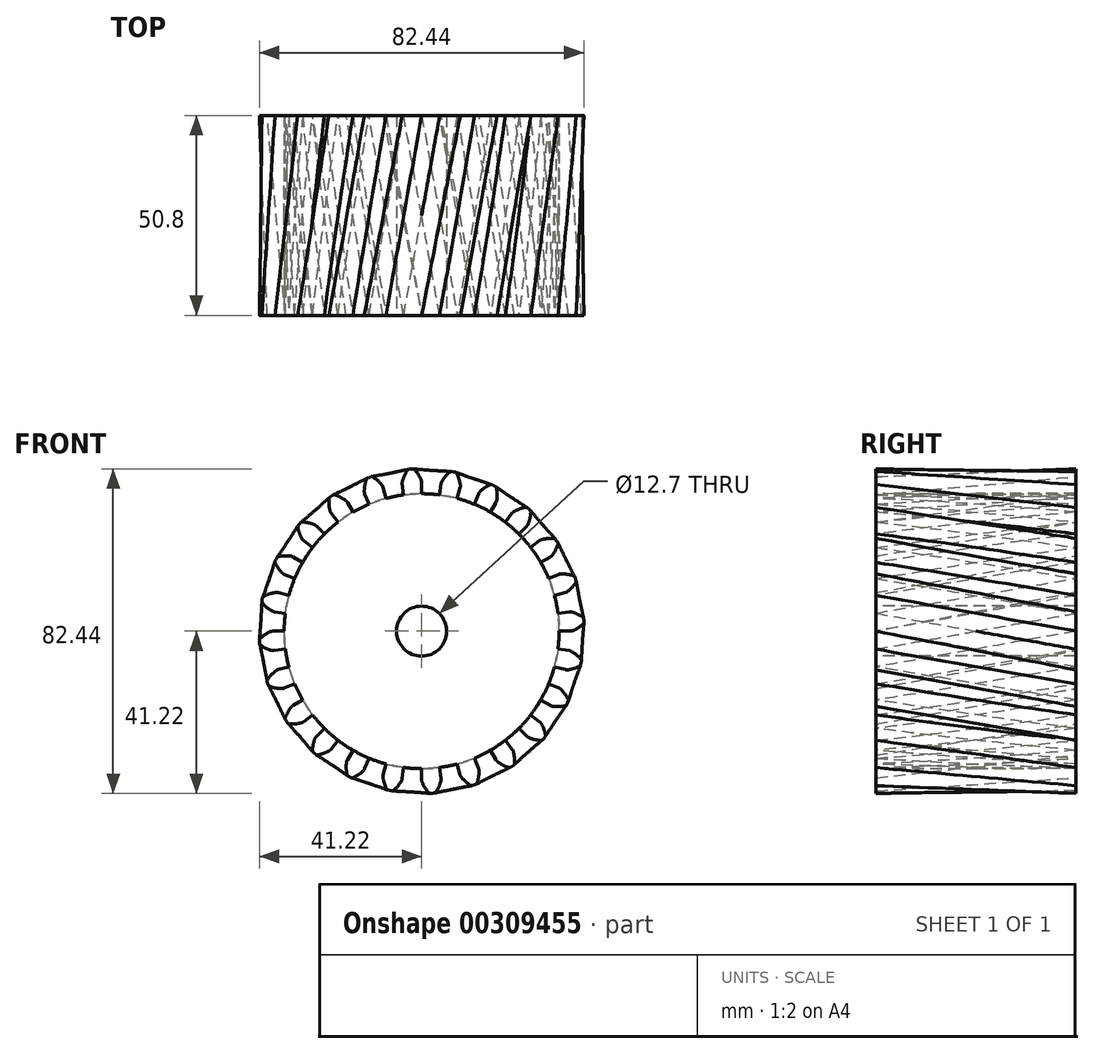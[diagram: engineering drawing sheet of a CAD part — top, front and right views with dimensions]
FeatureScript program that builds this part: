
annotation { "Feature Type Name" : "Feature", "Feature Type Description" : "" }
export const myFeature = defineFeature(function(context is Context, id is Id, definition is map)
    precondition{}
    {
        {
            var Q0;
            Q0=qCreatedBy(makeId("Front.planeOp"),FACE);
            var sketch = newSketch(context, id + "F0", { "sketchPlane" : qUnion([Q0])});
            skCircle(sketch, "E0", {"center": v(0, 0) * mm, "radius": 34.92 * mm});
            skArc(sketch, "E1", {"start": v(-0.13, 38.42) * mm, "mid": v(-0.86, 39.8) * mm, "end": v(-1.8, 41.05) * mm});
            skLineSegment(sketch, "E2", {"start": v(-2.2, 41.22) * mm, "end": v(-2.7, 41.2) * mm});
            skLineSegment(sketch, "E3", {"start": v(0, 37.79) * mm, "end": v(0, 34.92) * mm});
            skLineSegment(sketch, "E4.MirrorCS", {"start": v(-3.2, 41.15) * mm, "end": v(-2.7, 41.2) * mm});
            skArc(sketch, "E5.MirrorCS", {"start": v(-4.89, 38.1) * mm, "mid": v(-4.34, 39.57) * mm, "end": v(-3.57, 40.93) * mm});
            skLineSegment(sketch, "E6.MirrorCS", {"start": v(-4.93, 37.47) * mm, "end": v(-4.56, 34.63) * mm});
            skPoint(sketch, "E7.visualSharp", {"position": v(-4.97, 37.77) * mm});
            skArc(sketch, "E7.filletArc", {"start": v(-4.89, 38.1) * mm, "mid": v(-4.94, 37.79) * mm, "end": v(-4.93, 37.47) * mm});
            skPoint(sketch, "E8.visualSharp", {"position": v(0, 38.1) * mm});
            skArc(sketch, "E8.filletArc", {"start": v(0, 37.79) * mm, "mid": v(-0.03, 38.1) * mm, "end": v(-0.13, 38.42) * mm});
            skPoint(sketch, "E9.visualSharp", {"position": v(-3.43, 41.13) * mm});
            skArc(sketch, "E9.filletArc", {"start": v(-3.2, 41.15) * mm, "mid": v(-3.4, 41.09) * mm, "end": v(-3.57, 40.93) * mm});
            skPoint(sketch, "E10.visualSharp", {"position": v(-1.97, 41.23) * mm});
            skArc(sketch, "E10.filletArc", {"start": v(-1.8, 41.05) * mm, "mid": v(-1.99, 41.18) * mm, "end": v(-2.2, 41.22) * mm});
            skSolve(sketch);
        }
        {
            var Q0;
            Q0=qCreatedBy(makeId("Front.planeOp"),FACE);
            cPlane(context, id + "F1", {"entities" : qUnion([Q0]), "cplaneType" : CPlaneType.OFFSET, "offset" : 50.8 * mm, "width" : 152.4 * mm, "height" : 152.4 * mm});
        }
        {
            var Q0;
            Q0=qCreatedBy(id+"F1.planeOp",FACE);
            var sketch = newSketch(context, id + "F2", { "sketchPlane" : qUnion([Q0])});
            skCircle(sketch, "E11", {"center": v(0, 0) * mm, "radius": 34.92 * mm});
            skArc(sketch, "E12", {"start": v(-0.13, 38.42) * mm, "mid": v(-0.86, 39.8) * mm, "end": v(-1.8, 41.05) * mm});
            skLineSegment(sketch, "E13", {"start": v(-2.2, 41.22) * mm, "end": v(-2.7, 41.2) * mm});
            skLineSegment(sketch, "E14", {"start": v(0, 37.79) * mm, "end": v(0, 34.92) * mm});
            skLineSegment(sketch, "E15.MirrorCS", {"start": v(-3.2, 41.15) * mm, "end": v(-2.7, 41.2) * mm});
            skArc(sketch, "E16.MirrorCS", {"start": v(-4.89, 38.1) * mm, "mid": v(-4.34, 39.57) * mm, "end": v(-3.57, 40.93) * mm});
            skLineSegment(sketch, "E17.MirrorCS", {"start": v(-4.93, 37.47) * mm, "end": v(-4.56, 34.63) * mm});
            skPoint(sketch, "E18.visualSharp", {"position": v(-4.97, 37.77) * mm});
            skArc(sketch, "E18.filletArc", {"start": v(-4.89, 38.1) * mm, "mid": v(-4.94, 37.79) * mm, "end": v(-4.93, 37.47) * mm});
            skPoint(sketch, "E19.visualSharp", {"position": v(0, 38.1) * mm});
            skArc(sketch, "E19.filletArc", {"start": v(0, 37.79) * mm, "mid": v(-0.03, 38.1) * mm, "end": v(-0.13, 38.42) * mm});
            skPoint(sketch, "E20.visualSharp", {"position": v(-3.43, 41.13) * mm});
            skArc(sketch, "E20.filletArc", {"start": v(-3.2, 41.15) * mm, "mid": v(-3.4, 41.09) * mm, "end": v(-3.57, 40.93) * mm});
            skPoint(sketch, "E21.visualSharp", {"position": v(-1.97, 41.23) * mm});
            skArc(sketch, "E21.filletArc", {"start": v(-1.8, 41.05) * mm, "mid": v(-1.99, 41.18) * mm, "end": v(-2.2, 41.22) * mm});
            skLineSegment(sketch, "E22.1.0", {"start": v(-13.73, 38.92) * mm, "end": v(-13.27, 39.1) * mm});
            skLineSegment(sketch, "E22.1.1", {"start": v(-12.8, 39.24) * mm, "end": v(-13.27, 39.1) * mm});
            skArc(sketch, "E22.1.2", {"start": v(-13.73, 38.92) * mm, "mid": v(-13.92, 38.8) * mm, "end": v(-14.04, 38.62) * mm});
            skArc(sketch, "E22.1.3", {"start": v(-12.37, 39.18) * mm, "mid": v(-12.58, 39.26) * mm, "end": v(-12.8, 39.24) * mm});
            skArc(sketch, "E22.1.4", {"start": v(-14.58, 35.54) * mm, "mid": v(-14.44, 37.1) * mm, "end": v(-14.04, 38.62) * mm});
            skArc(sketch, "E22.1.5", {"start": v(-10.07, 37.07) * mm, "mid": v(-11.13, 38.22) * mm, "end": v(-12.37, 39.18) * mm});
            skArc(sketch, "E22.1.6", {"start": v(-14.58, 35.54) * mm, "mid": v(-14.55, 35.22) * mm, "end": v(-14.46, 34.91) * mm});
            skArc(sketch, "E22.1.7", {"start": v(-9.78, 36.5) * mm, "mid": v(-9.9, 36.8) * mm, "end": v(-10.07, 37.07) * mm});
            skLineSegment(sketch, "E22.1.8", {"start": v(-9.78, 36.5) * mm, "end": v(-9.04, 33.73) * mm});
            skLineSegment(sketch, "E22.1.9", {"start": v(-14.46, 34.91) * mm, "end": v(-13.37, 32.27) * mm});
            skLineSegment(sketch, "E22.2.0", {"start": v(-23.34, 34.04) * mm, "end": v(-22.93, 34.32) * mm});
            skLineSegment(sketch, "E22.2.1", {"start": v(-22.52, 34.6) * mm, "end": v(-22.93, 34.32) * mm});
            skArc(sketch, "E22.2.2", {"start": v(-23.34, 34.04) * mm, "mid": v(-23.49, 33.88) * mm, "end": v(-23.56, 33.67) * mm});
            skArc(sketch, "E22.2.3", {"start": v(-22.09, 34.65) * mm, "mid": v(-22.31, 34.67) * mm, "end": v(-22.52, 34.6) * mm});
            skArc(sketch, "E22.2.4", {"start": v(-23.28, 30.56) * mm, "mid": v(-23.55, 32.1) * mm, "end": v(-23.56, 33.67) * mm});
            skArc(sketch, "E22.2.5", {"start": v(-19.32, 33.2) * mm, "mid": v(-20.64, 34.04) * mm, "end": v(-22.09, 34.65) * mm});
            skArc(sketch, "E22.2.6", {"start": v(-23.28, 30.56) * mm, "mid": v(-23.17, 30.25) * mm, "end": v(-23, 29.98) * mm});
            skArc(sketch, "E22.2.7", {"start": v(-18.9, 32.73) * mm, "mid": v(-19.08, 32.99) * mm, "end": v(-19.32, 33.2) * mm});
            skLineSegment(sketch, "E22.2.8", {"start": v(-18.9, 32.73) * mm, "end": v(-17.46, 30.25) * mm});
            skLineSegment(sketch, "E22.2.9", {"start": v(-23, 29.98) * mm, "end": v(-21.26, 27.7) * mm});
            skLineSegment(sketch, "E22.3.0", {"start": v(-31.35, 26.84) * mm, "end": v(-31.04, 27.22) * mm});
            skLineSegment(sketch, "E22.3.1", {"start": v(-30.7, 27.58) * mm, "end": v(-31.04, 27.22) * mm});
            skArc(sketch, "E22.3.2", {"start": v(-31.35, 26.84) * mm, "mid": v(-31.46, 26.65) * mm, "end": v(-31.47, 26.42) * mm});
            skArc(sketch, "E22.3.3", {"start": v(-30.3, 27.75) * mm, "mid": v(-30.52, 27.71) * mm, "end": v(-30.7, 27.58) * mm});
            skArc(sketch, "E22.3.4", {"start": v(-30.4, 23.49) * mm, "mid": v(-31.05, 24.91) * mm, "end": v(-31.47, 26.42) * mm});
            skArc(sketch, "E22.3.5", {"start": v(-27.26, 27.07) * mm, "mid": v(-28.75, 27.54) * mm, "end": v(-30.3, 27.75) * mm});
            skArc(sketch, "E22.3.6", {"start": v(-30.4, 23.49) * mm, "mid": v(-30.21, 23.22) * mm, "end": v(-29.98, 23) * mm});
            skArc(sketch, "E22.3.7", {"start": v(-26.72, 26.72) * mm, "mid": v(-26.97, 26.92) * mm, "end": v(-27.26, 27.07) * mm});
            skLineSegment(sketch, "E22.3.8", {"start": v(-26.72, 26.72) * mm, "end": v(-24.7, 24.7) * mm});
            skLineSegment(sketch, "E22.3.9", {"start": v(-29.98, 23) * mm, "end": v(-27.7, 21.26) * mm});
            skLineSegment(sketch, "E22.4.0", {"start": v(-37.23, 17.81) * mm, "end": v(-37.02, 18.26) * mm});
            skLineSegment(sketch, "E22.4.1", {"start": v(-36.8, 18.7) * mm, "end": v(-37.02, 18.26) * mm});
            skArc(sketch, "E22.4.2", {"start": v(-37.23, 17.81) * mm, "mid": v(-37.28, 17.6) * mm, "end": v(-37.23, 17.38) * mm});
            skArc(sketch, "E22.4.3", {"start": v(-36.45, 18.96) * mm, "mid": v(-36.66, 18.87) * mm, "end": v(-36.8, 18.7) * mm});
            skArc(sketch, "E22.4.4", {"start": v(-35.44, 14.82) * mm, "mid": v(-36.44, 16.02) * mm, "end": v(-37.23, 17.38) * mm});
            skArc(sketch, "E22.4.5", {"start": v(-33.33, 19.1) * mm, "mid": v(-34.9, 19.16) * mm, "end": v(-36.45, 18.96) * mm});
            skArc(sketch, "E22.4.6", {"start": v(-35.44, 14.82) * mm, "mid": v(-35.2, 14.61) * mm, "end": v(-34.91, 14.46) * mm});
            skArc(sketch, "E22.4.7", {"start": v(-32.73, 18.9) * mm, "mid": v(-33.02, 19.03) * mm, "end": v(-33.33, 19.1) * mm});
            skLineSegment(sketch, "E22.4.8", {"start": v(-32.73, 18.9) * mm, "end": v(-30.25, 17.46) * mm});
            skLineSegment(sketch, "E22.4.9", {"start": v(-34.91, 14.46) * mm, "end": v(-32.27, 13.37) * mm});
            skLineSegment(sketch, "E22.5.0", {"start": v(-40.58, 7.57) * mm, "end": v(-40.49, 8.05) * mm});
            skLineSegment(sketch, "E22.5.1", {"start": v(-40.38, 8.53) * mm, "end": v(-40.49, 8.05) * mm});
            skArc(sketch, "E22.5.2", {"start": v(-40.58, 7.57) * mm, "mid": v(-40.57, 7.35) * mm, "end": v(-40.46, 7.15) * mm});
            skArc(sketch, "E22.5.3", {"start": v(-40.12, 8.88) * mm, "mid": v(-40.29, 8.74) * mm, "end": v(-40.38, 8.53) * mm});
            skArc(sketch, "E22.5.4", {"start": v(-38.07, 5.14) * mm, "mid": v(-39.35, 6.05) * mm, "end": v(-40.46, 7.15) * mm});
            skArc(sketch, "E22.5.5", {"start": v(-37.14, 9.82) * mm, "mid": v(-38.67, 9.47) * mm, "end": v(-40.12, 8.88) * mm});
            skArc(sketch, "E22.5.6", {"start": v(-38.07, 5.14) * mm, "mid": v(-37.78, 5) * mm, "end": v(-37.47, 4.93) * mm});
            skArc(sketch, "E22.5.7", {"start": v(-36.5, 9.78) * mm, "mid": v(-36.82, 9.83) * mm, "end": v(-37.14, 9.82) * mm});
            skLineSegment(sketch, "E22.5.8", {"start": v(-36.5, 9.78) * mm, "end": v(-33.73, 9.04) * mm});
            skLineSegment(sketch, "E22.5.9", {"start": v(-37.47, 4.93) * mm, "end": v(-34.63, 4.56) * mm});
            skLineSegment(sketch, "E22.6.0", {"start": v(-41.15, -3.2) * mm, "end": v(-41.2, -2.7) * mm});
            skLineSegment(sketch, "E22.6.1", {"start": v(-41.22, -2.2) * mm, "end": v(-41.2, -2.7) * mm});
            skArc(sketch, "E22.6.2", {"start": v(-41.15, -3.2) * mm, "mid": v(-41.09, -3.4) * mm, "end": v(-40.93, -3.57) * mm});
            skArc(sketch, "E22.6.3", {"start": v(-41.05, -1.8) * mm, "mid": v(-41.18, -1.99) * mm, "end": v(-41.22, -2.2) * mm});
            skArc(sketch, "E22.6.4", {"start": v(-38.1, -4.89) * mm, "mid": v(-39.57, -4.34) * mm, "end": v(-40.93, -3.57) * mm});
            skArc(sketch, "E22.6.5", {"start": v(-38.42, -0.13) * mm, "mid": v(-39.8, -0.86) * mm, "end": v(-41.05, -1.8) * mm});
            skArc(sketch, "E22.6.6", {"start": v(-38.1, -4.89) * mm, "mid": v(-37.79, -4.94) * mm, "end": v(-37.47, -4.93) * mm});
            skArc(sketch, "E22.6.7", {"start": v(-37.79, 0) * mm, "mid": v(-38.1, -0.03) * mm, "end": v(-38.42, -0.13) * mm});
            skLineSegment(sketch, "E22.6.8", {"start": v(-37.79, 0) * mm, "end": v(-34.92, 0) * mm});
            skLineSegment(sketch, "E22.6.9", {"start": v(-37.47, -4.93) * mm, "end": v(-34.63, -4.56) * mm});
            skLineSegment(sketch, "E22.7.0", {"start": v(-38.92, -13.73) * mm, "end": v(-39.1, -13.27) * mm});
            skLineSegment(sketch, "E22.7.1", {"start": v(-39.24, -12.8) * mm, "end": v(-39.1, -13.27) * mm});
            skArc(sketch, "E22.7.2", {"start": v(-38.92, -13.73) * mm, "mid": v(-38.8, -13.92) * mm, "end": v(-38.62, -14.04) * mm});
            skArc(sketch, "E22.7.3", {"start": v(-39.18, -12.37) * mm, "mid": v(-39.26, -12.58) * mm, "end": v(-39.24, -12.8) * mm});
            skArc(sketch, "E22.7.4", {"start": v(-35.54, -14.58) * mm, "mid": v(-37.1, -14.44) * mm, "end": v(-38.62, -14.04) * mm});
            skArc(sketch, "E22.7.5", {"start": v(-37.07, -10.07) * mm, "mid": v(-38.22, -11.13) * mm, "end": v(-39.18, -12.37) * mm});
            skArc(sketch, "E22.7.6", {"start": v(-35.54, -14.58) * mm, "mid": v(-35.22, -14.55) * mm, "end": v(-34.91, -14.46) * mm});
            skArc(sketch, "E22.7.7", {"start": v(-36.5, -9.78) * mm, "mid": v(-36.8, -9.9) * mm, "end": v(-37.07, -10.07) * mm});
            skLineSegment(sketch, "E22.7.8", {"start": v(-36.5, -9.78) * mm, "end": v(-33.73, -9.04) * mm});
            skLineSegment(sketch, "E22.7.9", {"start": v(-34.91, -14.46) * mm, "end": v(-32.27, -13.37) * mm});
            skLineSegment(sketch, "E22.8.0", {"start": v(-34.04, -23.34) * mm, "end": v(-34.32, -22.93) * mm});
            skLineSegment(sketch, "E22.8.1", {"start": v(-34.6, -22.52) * mm, "end": v(-34.32, -22.93) * mm});
            skArc(sketch, "E22.8.2", {"start": v(-34.04, -23.34) * mm, "mid": v(-33.88, -23.49) * mm, "end": v(-33.67, -23.56) * mm});
            skArc(sketch, "E22.8.3", {"start": v(-34.65, -22.09) * mm, "mid": v(-34.67, -22.31) * mm, "end": v(-34.6, -22.52) * mm});
            skArc(sketch, "E22.8.4", {"start": v(-30.56, -23.28) * mm, "mid": v(-32.1, -23.55) * mm, "end": v(-33.67, -23.56) * mm});
            skArc(sketch, "E22.8.5", {"start": v(-33.2, -19.32) * mm, "mid": v(-34.04, -20.64) * mm, "end": v(-34.65, -22.09) * mm});
            skArc(sketch, "E22.8.6", {"start": v(-30.56, -23.28) * mm, "mid": v(-30.25, -23.17) * mm, "end": v(-29.98, -23) * mm});
            skArc(sketch, "E22.8.7", {"start": v(-32.73, -18.9) * mm, "mid": v(-32.99, -19.08) * mm, "end": v(-33.2, -19.32) * mm});
            skLineSegment(sketch, "E22.8.8", {"start": v(-32.73, -18.9) * mm, "end": v(-30.25, -17.46) * mm});
            skLineSegment(sketch, "E22.8.9", {"start": v(-29.98, -23) * mm, "end": v(-27.7, -21.26) * mm});
            skLineSegment(sketch, "E22.9.0", {"start": v(-26.84, -31.35) * mm, "end": v(-27.22, -31.04) * mm});
            skLineSegment(sketch, "E22.9.1", {"start": v(-27.58, -30.7) * mm, "end": v(-27.22, -31.04) * mm});
            skArc(sketch, "E22.9.2", {"start": v(-26.84, -31.35) * mm, "mid": v(-26.65, -31.46) * mm, "end": v(-26.42, -31.47) * mm});
            skArc(sketch, "E22.9.3", {"start": v(-27.75, -30.3) * mm, "mid": v(-27.71, -30.52) * mm, "end": v(-27.58, -30.7) * mm});
            skArc(sketch, "E22.9.4", {"start": v(-23.49, -30.4) * mm, "mid": v(-24.91, -31.05) * mm, "end": v(-26.42, -31.47) * mm});
            skArc(sketch, "E22.9.5", {"start": v(-27.07, -27.26) * mm, "mid": v(-27.54, -28.75) * mm, "end": v(-27.75, -30.3) * mm});
            skArc(sketch, "E22.9.6", {"start": v(-23.49, -30.4) * mm, "mid": v(-23.22, -30.21) * mm, "end": v(-23, -29.98) * mm});
            skArc(sketch, "E22.9.7", {"start": v(-26.72, -26.72) * mm, "mid": v(-26.92, -26.97) * mm, "end": v(-27.07, -27.26) * mm});
            skLineSegment(sketch, "E22.9.8", {"start": v(-26.72, -26.72) * mm, "end": v(-24.7, -24.7) * mm});
            skLineSegment(sketch, "E22.9.9", {"start": v(-23, -29.98) * mm, "end": v(-21.26, -27.7) * mm});
            skLineSegment(sketch, "E22.10.0", {"start": v(-17.81, -37.23) * mm, "end": v(-18.26, -37.02) * mm});
            skLineSegment(sketch, "E22.10.1", {"start": v(-18.7, -36.8) * mm, "end": v(-18.26, -37.02) * mm});
            skArc(sketch, "E22.10.2", {"start": v(-17.81, -37.23) * mm, "mid": v(-17.6, -37.28) * mm, "end": v(-17.38, -37.23) * mm});
            skArc(sketch, "E22.10.3", {"start": v(-18.96, -36.45) * mm, "mid": v(-18.87, -36.66) * mm, "end": v(-18.7, -36.8) * mm});
            skArc(sketch, "E22.10.4", {"start": v(-14.82, -35.44) * mm, "mid": v(-16.02, -36.44) * mm, "end": v(-17.38, -37.23) * mm});
            skArc(sketch, "E22.10.5", {"start": v(-19.1, -33.33) * mm, "mid": v(-19.16, -34.9) * mm, "end": v(-18.96, -36.45) * mm});
            skArc(sketch, "E22.10.6", {"start": v(-14.82, -35.44) * mm, "mid": v(-14.61, -35.2) * mm, "end": v(-14.46, -34.91) * mm});
            skArc(sketch, "E22.10.7", {"start": v(-18.9, -32.73) * mm, "mid": v(-19.03, -33.02) * mm, "end": v(-19.1, -33.33) * mm});
            skLineSegment(sketch, "E22.10.8", {"start": v(-18.9, -32.73) * mm, "end": v(-17.46, -30.25) * mm});
            skLineSegment(sketch, "E22.10.9", {"start": v(-14.46, -34.91) * mm, "end": v(-13.37, -32.27) * mm});
            skLineSegment(sketch, "E22.11.0", {"start": v(-7.57, -40.58) * mm, "end": v(-8.05, -40.49) * mm});
            skLineSegment(sketch, "E22.11.1", {"start": v(-8.53, -40.38) * mm, "end": v(-8.05, -40.49) * mm});
            skArc(sketch, "E22.11.2", {"start": v(-7.57, -40.58) * mm, "mid": v(-7.35, -40.57) * mm, "end": v(-7.15, -40.46) * mm});
            skArc(sketch, "E22.11.3", {"start": v(-8.88, -40.12) * mm, "mid": v(-8.74, -40.29) * mm, "end": v(-8.53, -40.38) * mm});
            skArc(sketch, "E22.11.4", {"start": v(-5.14, -38.07) * mm, "mid": v(-6.05, -39.35) * mm, "end": v(-7.15, -40.46) * mm});
            skArc(sketch, "E22.11.5", {"start": v(-9.82, -37.14) * mm, "mid": v(-9.47, -38.67) * mm, "end": v(-8.88, -40.12) * mm});
            skArc(sketch, "E22.11.6", {"start": v(-5.14, -38.07) * mm, "mid": v(-5, -37.78) * mm, "end": v(-4.93, -37.47) * mm});
            skArc(sketch, "E22.11.7", {"start": v(-9.78, -36.5) * mm, "mid": v(-9.83, -36.82) * mm, "end": v(-9.82, -37.14) * mm});
            skLineSegment(sketch, "E22.11.8", {"start": v(-9.78, -36.5) * mm, "end": v(-9.04, -33.73) * mm});
            skLineSegment(sketch, "E22.11.9", {"start": v(-4.93, -37.47) * mm, "end": v(-4.56, -34.63) * mm});
            skLineSegment(sketch, "E22.12.0", {"start": v(3.2, -41.15) * mm, "end": v(2.7, -41.2) * mm});
            skLineSegment(sketch, "E22.12.1", {"start": v(2.2, -41.22) * mm, "end": v(2.7, -41.2) * mm});
            skArc(sketch, "E22.12.2", {"start": v(3.2, -41.15) * mm, "mid": v(3.4, -41.09) * mm, "end": v(3.57, -40.93) * mm});
            skArc(sketch, "E22.12.3", {"start": v(1.8, -41.05) * mm, "mid": v(1.99, -41.18) * mm, "end": v(2.2, -41.22) * mm});
            skArc(sketch, "E22.12.4", {"start": v(4.89, -38.1) * mm, "mid": v(4.34, -39.57) * mm, "end": v(3.57, -40.93) * mm});
            skArc(sketch, "E22.12.5", {"start": v(0.13, -38.42) * mm, "mid": v(0.86, -39.8) * mm, "end": v(1.8, -41.05) * mm});
            skArc(sketch, "E22.12.6", {"start": v(4.89, -38.1) * mm, "mid": v(4.94, -37.79) * mm, "end": v(4.93, -37.47) * mm});
            skArc(sketch, "E22.12.7", {"start": v(0, -37.79) * mm, "mid": v(0.03, -38.1) * mm, "end": v(0.13, -38.42) * mm});
            skLineSegment(sketch, "E22.12.8", {"start": v(0, -37.79) * mm, "end": v(0, -34.92) * mm});
            skLineSegment(sketch, "E22.12.9", {"start": v(4.93, -37.47) * mm, "end": v(4.56, -34.63) * mm});
            skLineSegment(sketch, "E22.13.0", {"start": v(13.73, -38.92) * mm, "end": v(13.27, -39.1) * mm});
            skLineSegment(sketch, "E22.13.1", {"start": v(12.8, -39.24) * mm, "end": v(13.27, -39.1) * mm});
            skArc(sketch, "E22.13.2", {"start": v(13.73, -38.92) * mm, "mid": v(13.92, -38.8) * mm, "end": v(14.04, -38.62) * mm});
            skArc(sketch, "E22.13.3", {"start": v(12.37, -39.18) * mm, "mid": v(12.58, -39.26) * mm, "end": v(12.8, -39.24) * mm});
            skArc(sketch, "E22.13.4", {"start": v(14.58, -35.54) * mm, "mid": v(14.44, -37.1) * mm, "end": v(14.04, -38.62) * mm});
            skArc(sketch, "E22.13.5", {"start": v(10.07, -37.07) * mm, "mid": v(11.13, -38.22) * mm, "end": v(12.37, -39.18) * mm});
            skArc(sketch, "E22.13.6", {"start": v(14.58, -35.54) * mm, "mid": v(14.55, -35.22) * mm, "end": v(14.46, -34.91) * mm});
            skArc(sketch, "E22.13.7", {"start": v(9.78, -36.5) * mm, "mid": v(9.9, -36.8) * mm, "end": v(10.07, -37.07) * mm});
            skLineSegment(sketch, "E22.13.8", {"start": v(9.78, -36.5) * mm, "end": v(9.04, -33.73) * mm});
            skLineSegment(sketch, "E22.13.9", {"start": v(14.46, -34.91) * mm, "end": v(13.37, -32.27) * mm});
            skLineSegment(sketch, "E22.14.0", {"start": v(23.34, -34.04) * mm, "end": v(22.93, -34.32) * mm});
            skLineSegment(sketch, "E22.14.1", {"start": v(22.52, -34.6) * mm, "end": v(22.93, -34.32) * mm});
            skArc(sketch, "E22.14.2", {"start": v(23.34, -34.04) * mm, "mid": v(23.49, -33.88) * mm, "end": v(23.56, -33.67) * mm});
            skArc(sketch, "E22.14.3", {"start": v(22.09, -34.65) * mm, "mid": v(22.31, -34.67) * mm, "end": v(22.52, -34.6) * mm});
            skArc(sketch, "E22.14.4", {"start": v(23.28, -30.56) * mm, "mid": v(23.55, -32.1) * mm, "end": v(23.56, -33.67) * mm});
            skArc(sketch, "E22.14.5", {"start": v(19.32, -33.2) * mm, "mid": v(20.64, -34.04) * mm, "end": v(22.09, -34.65) * mm});
            skArc(sketch, "E22.14.6", {"start": v(23.28, -30.56) * mm, "mid": v(23.17, -30.25) * mm, "end": v(23, -29.98) * mm});
            skArc(sketch, "E22.14.7", {"start": v(18.9, -32.73) * mm, "mid": v(19.08, -32.99) * mm, "end": v(19.32, -33.2) * mm});
            skLineSegment(sketch, "E22.14.8", {"start": v(18.9, -32.73) * mm, "end": v(17.46, -30.25) * mm});
            skLineSegment(sketch, "E22.14.9", {"start": v(23, -29.98) * mm, "end": v(21.26, -27.7) * mm});
            skLineSegment(sketch, "E22.15.0", {"start": v(31.35, -26.84) * mm, "end": v(31.04, -27.22) * mm});
            skLineSegment(sketch, "E22.15.1", {"start": v(30.7, -27.58) * mm, "end": v(31.04, -27.22) * mm});
            skArc(sketch, "E22.15.2", {"start": v(31.35, -26.84) * mm, "mid": v(31.46, -26.65) * mm, "end": v(31.47, -26.42) * mm});
            skArc(sketch, "E22.15.3", {"start": v(30.3, -27.75) * mm, "mid": v(30.52, -27.71) * mm, "end": v(30.7, -27.58) * mm});
            skArc(sketch, "E22.15.4", {"start": v(30.4, -23.49) * mm, "mid": v(31.05, -24.91) * mm, "end": v(31.47, -26.42) * mm});
            skArc(sketch, "E22.15.5", {"start": v(27.26, -27.07) * mm, "mid": v(28.75, -27.54) * mm, "end": v(30.3, -27.75) * mm});
            skArc(sketch, "E22.15.6", {"start": v(30.4, -23.49) * mm, "mid": v(30.21, -23.22) * mm, "end": v(29.98, -23) * mm});
            skArc(sketch, "E22.15.7", {"start": v(26.72, -26.72) * mm, "mid": v(26.97, -26.92) * mm, "end": v(27.26, -27.07) * mm});
            skLineSegment(sketch, "E22.15.8", {"start": v(26.72, -26.72) * mm, "end": v(24.7, -24.7) * mm});
            skLineSegment(sketch, "E22.15.9", {"start": v(29.98, -23) * mm, "end": v(27.7, -21.26) * mm});
            skLineSegment(sketch, "E22.16.0", {"start": v(37.23, -17.81) * mm, "end": v(37.02, -18.26) * mm});
            skLineSegment(sketch, "E22.16.1", {"start": v(36.8, -18.7) * mm, "end": v(37.02, -18.26) * mm});
            skArc(sketch, "E22.16.2", {"start": v(37.23, -17.81) * mm, "mid": v(37.28, -17.6) * mm, "end": v(37.23, -17.38) * mm});
            skArc(sketch, "E22.16.3", {"start": v(36.45, -18.96) * mm, "mid": v(36.66, -18.87) * mm, "end": v(36.8, -18.7) * mm});
            skArc(sketch, "E22.16.4", {"start": v(35.44, -14.82) * mm, "mid": v(36.44, -16.02) * mm, "end": v(37.23, -17.38) * mm});
            skArc(sketch, "E22.16.5", {"start": v(33.33, -19.1) * mm, "mid": v(34.9, -19.16) * mm, "end": v(36.45, -18.96) * mm});
            skArc(sketch, "E22.16.6", {"start": v(35.44, -14.82) * mm, "mid": v(35.2, -14.61) * mm, "end": v(34.91, -14.46) * mm});
            skArc(sketch, "E22.16.7", {"start": v(32.73, -18.9) * mm, "mid": v(33.02, -19.03) * mm, "end": v(33.33, -19.1) * mm});
            skLineSegment(sketch, "E22.16.8", {"start": v(32.73, -18.9) * mm, "end": v(30.25, -17.46) * mm});
            skLineSegment(sketch, "E22.16.9", {"start": v(34.91, -14.46) * mm, "end": v(32.27, -13.37) * mm});
            skLineSegment(sketch, "E22.17.0", {"start": v(40.58, -7.57) * mm, "end": v(40.49, -8.05) * mm});
            skLineSegment(sketch, "E22.17.1", {"start": v(40.38, -8.53) * mm, "end": v(40.49, -8.05) * mm});
            skArc(sketch, "E22.17.2", {"start": v(40.58, -7.57) * mm, "mid": v(40.57, -7.35) * mm, "end": v(40.46, -7.15) * mm});
            skArc(sketch, "E22.17.3", {"start": v(40.12, -8.88) * mm, "mid": v(40.29, -8.74) * mm, "end": v(40.38, -8.53) * mm});
            skArc(sketch, "E22.17.4", {"start": v(38.07, -5.14) * mm, "mid": v(39.35, -6.05) * mm, "end": v(40.46, -7.15) * mm});
            skArc(sketch, "E22.17.5", {"start": v(37.14, -9.82) * mm, "mid": v(38.67, -9.47) * mm, "end": v(40.12, -8.88) * mm});
            skArc(sketch, "E22.17.6", {"start": v(38.07, -5.14) * mm, "mid": v(37.78, -5) * mm, "end": v(37.47, -4.93) * mm});
            skArc(sketch, "E22.17.7", {"start": v(36.5, -9.78) * mm, "mid": v(36.82, -9.83) * mm, "end": v(37.14, -9.82) * mm});
            skLineSegment(sketch, "E22.17.8", {"start": v(36.5, -9.78) * mm, "end": v(33.73, -9.04) * mm});
            skLineSegment(sketch, "E22.17.9", {"start": v(37.47, -4.93) * mm, "end": v(34.63, -4.56) * mm});
            skLineSegment(sketch, "E22.18.0", {"start": v(41.15, 3.2) * mm, "end": v(41.2, 2.7) * mm});
            skLineSegment(sketch, "E22.18.1", {"start": v(41.22, 2.2) * mm, "end": v(41.2, 2.7) * mm});
            skArc(sketch, "E22.18.2", {"start": v(41.15, 3.2) * mm, "mid": v(41.09, 3.4) * mm, "end": v(40.93, 3.57) * mm});
            skArc(sketch, "E22.18.3", {"start": v(41.05, 1.8) * mm, "mid": v(41.18, 1.99) * mm, "end": v(41.22, 2.2) * mm});
            skArc(sketch, "E22.18.4", {"start": v(38.1, 4.89) * mm, "mid": v(39.57, 4.34) * mm, "end": v(40.93, 3.57) * mm});
            skArc(sketch, "E22.18.5", {"start": v(38.42, 0.13) * mm, "mid": v(39.8, 0.86) * mm, "end": v(41.05, 1.8) * mm});
            skArc(sketch, "E22.18.6", {"start": v(38.1, 4.89) * mm, "mid": v(37.79, 4.94) * mm, "end": v(37.47, 4.93) * mm});
            skArc(sketch, "E22.18.7", {"start": v(37.79, 0) * mm, "mid": v(38.1, 0.03) * mm, "end": v(38.42, 0.13) * mm});
            skLineSegment(sketch, "E22.18.8", {"start": v(37.79, 0) * mm, "end": v(34.92, 0) * mm});
            skLineSegment(sketch, "E22.18.9", {"start": v(37.47, 4.93) * mm, "end": v(34.63, 4.56) * mm});
            skLineSegment(sketch, "E22.19.0", {"start": v(38.92, 13.73) * mm, "end": v(39.1, 13.27) * mm});
            skLineSegment(sketch, "E22.19.1", {"start": v(39.24, 12.8) * mm, "end": v(39.1, 13.27) * mm});
            skArc(sketch, "E22.19.2", {"start": v(38.92, 13.73) * mm, "mid": v(38.8, 13.92) * mm, "end": v(38.62, 14.04) * mm});
            skArc(sketch, "E22.19.3", {"start": v(39.18, 12.37) * mm, "mid": v(39.26, 12.58) * mm, "end": v(39.24, 12.8) * mm});
            skArc(sketch, "E22.19.4", {"start": v(35.54, 14.58) * mm, "mid": v(37.1, 14.44) * mm, "end": v(38.62, 14.04) * mm});
            skArc(sketch, "E22.19.5", {"start": v(37.07, 10.07) * mm, "mid": v(38.22, 11.13) * mm, "end": v(39.18, 12.37) * mm});
            skArc(sketch, "E22.19.6", {"start": v(35.54, 14.58) * mm, "mid": v(35.22, 14.55) * mm, "end": v(34.91, 14.46) * mm});
            skArc(sketch, "E22.19.7", {"start": v(36.5, 9.78) * mm, "mid": v(36.8, 9.9) * mm, "end": v(37.07, 10.07) * mm});
            skLineSegment(sketch, "E22.19.8", {"start": v(36.5, 9.78) * mm, "end": v(33.73, 9.04) * mm});
            skLineSegment(sketch, "E22.19.9", {"start": v(34.91, 14.46) * mm, "end": v(32.27, 13.37) * mm});
            skLineSegment(sketch, "E22.20.0", {"start": v(34.04, 23.34) * mm, "end": v(34.32, 22.93) * mm});
            skLineSegment(sketch, "E22.20.1", {"start": v(34.6, 22.52) * mm, "end": v(34.32, 22.93) * mm});
            skArc(sketch, "E22.20.2", {"start": v(34.04, 23.34) * mm, "mid": v(33.88, 23.49) * mm, "end": v(33.67, 23.56) * mm});
            skArc(sketch, "E22.20.3", {"start": v(34.65, 22.09) * mm, "mid": v(34.67, 22.31) * mm, "end": v(34.6, 22.52) * mm});
            skArc(sketch, "E22.20.4", {"start": v(30.56, 23.28) * mm, "mid": v(32.1, 23.55) * mm, "end": v(33.67, 23.56) * mm});
            skArc(sketch, "E22.20.5", {"start": v(33.2, 19.32) * mm, "mid": v(34.04, 20.64) * mm, "end": v(34.65, 22.09) * mm});
            skArc(sketch, "E22.20.6", {"start": v(30.56, 23.28) * mm, "mid": v(30.25, 23.17) * mm, "end": v(29.98, 23) * mm});
            skArc(sketch, "E22.20.7", {"start": v(32.73, 18.9) * mm, "mid": v(32.99, 19.08) * mm, "end": v(33.2, 19.32) * mm});
            skLineSegment(sketch, "E22.20.8", {"start": v(32.73, 18.9) * mm, "end": v(30.25, 17.46) * mm});
            skLineSegment(sketch, "E22.20.9", {"start": v(29.98, 23) * mm, "end": v(27.7, 21.26) * mm});
            skLineSegment(sketch, "E22.21.0", {"start": v(26.84, 31.35) * mm, "end": v(27.22, 31.04) * mm});
            skLineSegment(sketch, "E22.21.1", {"start": v(27.58, 30.7) * mm, "end": v(27.22, 31.04) * mm});
            skArc(sketch, "E22.21.2", {"start": v(26.84, 31.35) * mm, "mid": v(26.65, 31.46) * mm, "end": v(26.42, 31.47) * mm});
            skArc(sketch, "E22.21.3", {"start": v(27.75, 30.3) * mm, "mid": v(27.71, 30.52) * mm, "end": v(27.58, 30.7) * mm});
            skArc(sketch, "E22.21.4", {"start": v(23.49, 30.4) * mm, "mid": v(24.91, 31.05) * mm, "end": v(26.42, 31.47) * mm});
            skArc(sketch, "E22.21.5", {"start": v(27.07, 27.26) * mm, "mid": v(27.54, 28.75) * mm, "end": v(27.75, 30.3) * mm});
            skArc(sketch, "E22.21.6", {"start": v(23.49, 30.4) * mm, "mid": v(23.22, 30.21) * mm, "end": v(23, 29.98) * mm});
            skArc(sketch, "E22.21.7", {"start": v(26.72, 26.72) * mm, "mid": v(26.92, 26.97) * mm, "end": v(27.07, 27.26) * mm});
            skLineSegment(sketch, "E22.21.8", {"start": v(26.72, 26.72) * mm, "end": v(24.7, 24.7) * mm});
            skLineSegment(sketch, "E22.21.9", {"start": v(23, 29.98) * mm, "end": v(21.26, 27.7) * mm});
            skLineSegment(sketch, "E22.22.0", {"start": v(17.81, 37.23) * mm, "end": v(18.26, 37.02) * mm});
            skLineSegment(sketch, "E22.22.1", {"start": v(18.7, 36.8) * mm, "end": v(18.26, 37.02) * mm});
            skArc(sketch, "E22.22.2", {"start": v(17.81, 37.23) * mm, "mid": v(17.6, 37.28) * mm, "end": v(17.38, 37.23) * mm});
            skArc(sketch, "E22.22.3", {"start": v(18.96, 36.45) * mm, "mid": v(18.87, 36.66) * mm, "end": v(18.7, 36.8) * mm});
            skArc(sketch, "E22.22.4", {"start": v(14.82, 35.44) * mm, "mid": v(16.02, 36.44) * mm, "end": v(17.38, 37.23) * mm});
            skArc(sketch, "E22.22.5", {"start": v(19.1, 33.33) * mm, "mid": v(19.16, 34.9) * mm, "end": v(18.96, 36.45) * mm});
            skArc(sketch, "E22.22.6", {"start": v(14.82, 35.44) * mm, "mid": v(14.61, 35.2) * mm, "end": v(14.46, 34.91) * mm});
            skArc(sketch, "E22.22.7", {"start": v(18.9, 32.73) * mm, "mid": v(19.03, 33.02) * mm, "end": v(19.1, 33.33) * mm});
            skLineSegment(sketch, "E22.22.8", {"start": v(18.9, 32.73) * mm, "end": v(17.46, 30.25) * mm});
            skLineSegment(sketch, "E22.22.9", {"start": v(14.46, 34.91) * mm, "end": v(13.37, 32.27) * mm});
            skLineSegment(sketch, "E22.23.0", {"start": v(7.57, 40.58) * mm, "end": v(8.05, 40.49) * mm});
            skLineSegment(sketch, "E22.23.1", {"start": v(8.53, 40.38) * mm, "end": v(8.05, 40.49) * mm});
            skArc(sketch, "E22.23.2", {"start": v(7.57, 40.58) * mm, "mid": v(7.35, 40.57) * mm, "end": v(7.15, 40.46) * mm});
            skArc(sketch, "E22.23.3", {"start": v(8.88, 40.12) * mm, "mid": v(8.74, 40.29) * mm, "end": v(8.53, 40.38) * mm});
            skArc(sketch, "E22.23.4", {"start": v(5.14, 38.07) * mm, "mid": v(6.05, 39.35) * mm, "end": v(7.15, 40.46) * mm});
            skArc(sketch, "E22.23.5", {"start": v(9.82, 37.14) * mm, "mid": v(9.47, 38.67) * mm, "end": v(8.88, 40.12) * mm});
            skArc(sketch, "E22.23.6", {"start": v(5.14, 38.07) * mm, "mid": v(5, 37.78) * mm, "end": v(4.93, 37.47) * mm});
            skArc(sketch, "E22.23.7", {"start": v(9.78, 36.5) * mm, "mid": v(9.83, 36.82) * mm, "end": v(9.82, 37.14) * mm});
            skLineSegment(sketch, "E22.23.8", {"start": v(9.78, 36.5) * mm, "end": v(9.04, 33.73) * mm});
            skLineSegment(sketch, "E22.23.9", {"start": v(4.93, 37.47) * mm, "end": v(4.56, 34.63) * mm});
            skSolve(sketch);
        }
        {
            var Q0;
            Q0=makeQuery(id+"F0.imprint","IMPRINT",FACE,{"disambiguationData":[TD([[makeQuery(id+"F0.imprint","IMPRINT",EDGE,{"derivedFrom":sQuery(id+"F0.wireOp",EDGE,"E1")}),1.0]])]});
            var Q1;
            Q1=makeQuery(id+"F2.imprint","IMPRINT",FACE,{"disambiguationData":[TD([[makeQuery(id+"F2.imprint","IMPRINT",EDGE,{"derivedFrom":sQuery(id+"F2.wireOp",EDGE,"E22.1.0")}),-1.0]])]});
            loft(context, id + "F3", {"sheetProfilesArray" : [{ "sheetProfileEntities" : qUnion([Q0]) }, { "sheetProfileEntities" : qUnion([Q1]) }]});
        }
        {
            var Q0;
            Q0=qCreatedBy(id+"F1.planeOp",FACE);
            var sketch = newSketch(context, id + "F4", { "sketchPlane" : qUnion([Q0])});
            skCircle(sketch, "E23", {"center": v(0, 0) * mm, "radius": 34.93 * mm});
            skSolve(sketch);
        }
        {
            var Q0;
            Q0 = qSketchRegion(id + "F4", true);
            var Q1;
            Q1=makeQuery(id+"F3.opLoft","CAP_FACE",FACE,{"disambiguationData":[OSD([makeQuery(id+"F0.imprint","IMPRINT",FACE,{"disambiguationData":[TD([[makeQuery(id+"F0.imprint","IMPRINT",EDGE,{"derivedFrom":sQuery(id+"F0.wireOp",EDGE,"E1")}),1.0]])]})])],"isStart":true});
            extrude(context, id + "F5", {"entities" : qUnion([Q0]), "operationType" : NewBodyOperationType.ADD, "endBound" : BoundingType.UP_TO_SURFACE, "oppositeDirection" : true, "endBoundEntityFace" : qUnion([Q1]), "depth" : 25.4 * mm});
        }
        {
            var Q0;
            Q0=makeQuery(id+"F3.opLoft","SWEPT_BODY",BODY,{"disambiguationData":[OSD([makeQuery(id+"F0.imprint","IMPRINT",FACE,{"disambiguationData":[TD([[makeQuery(id+"F0.imprint","IMPRINT",EDGE,{"derivedFrom":sQuery(id+"F0.wireOp",EDGE,"E1")}),1.0]])]}),makeQuery(id+"F2.imprint","IMPRINT",FACE,{"disambiguationData":[TD([[makeQuery(id+"F2.imprint","IMPRINT",EDGE,{"derivedFrom":sQuery(id+"F2.wireOp",EDGE,"E22.1.0")}),-1.0]])]})])]});
            var Q1;
            Q1=makeQuery(id+"F5.opExtrude","SWEPT_FACE",FACE,{"disambiguationData":[OSD([sQuery(id+"F4.wireOp",EDGE,"E23")])]});
            circularPattern(context, id + "F6", {"entities" : qUnion([Q0]), "axis" : qUnion([Q1]), "angle" : 360 * degree, "instanceCount" : 24, "equalSpace" : true});
        }
        {
            var Q0;
            Q0=makeQuery(id+"F3.opLoft","SWEPT_BODY",BODY,{"disambiguationData":[OSD([makeQuery(id+"F0.imprint","IMPRINT",FACE,{"disambiguationData":[TD([[makeQuery(id+"F0.imprint","IMPRINT",EDGE,{"derivedFrom":sQuery(id+"F0.wireOp",EDGE,"E1")}),1.0]])]}),makeQuery(id+"F2.imprint","IMPRINT",FACE,{"disambiguationData":[TD([[makeQuery(id+"F2.imprint","IMPRINT",EDGE,{"derivedFrom":sQuery(id+"F2.wireOp",EDGE,"E22.1.0")}),-1.0]])]})])]});
            var Q1;
            Q1=makeQuery(id+"F6.opPattern","COPY",BODY,{"derivedFrom":makeQuery(id+"F3.opLoft","SWEPT_BODY",BODY,{"disambiguationData":[OSD([makeQuery(id+"F0.imprint","IMPRINT",FACE,{"disambiguationData":[TD([[makeQuery(id+"F0.imprint","IMPRINT",EDGE,{"derivedFrom":sQuery(id+"F0.wireOp",EDGE,"E1")}),1.0]])]}),makeQuery(id+"F2.imprint","IMPRINT",FACE,{"disambiguationData":[TD([[makeQuery(id+"F2.imprint","IMPRINT",EDGE,{"derivedFrom":sQuery(id+"F2.wireOp",EDGE,"E22.1.0")}),-1.0]])]})])]}),"instanceName":"1"});
            var Q2;
            Q2=makeQuery(id+"F6.opPattern","COPY",BODY,{"derivedFrom":makeQuery(id+"F3.opLoft","SWEPT_BODY",BODY,{"disambiguationData":[OSD([makeQuery(id+"F0.imprint","IMPRINT",FACE,{"disambiguationData":[TD([[makeQuery(id+"F0.imprint","IMPRINT",EDGE,{"derivedFrom":sQuery(id+"F0.wireOp",EDGE,"E1")}),1.0]])]}),makeQuery(id+"F2.imprint","IMPRINT",FACE,{"disambiguationData":[TD([[makeQuery(id+"F2.imprint","IMPRINT",EDGE,{"derivedFrom":sQuery(id+"F2.wireOp",EDGE,"E22.1.0")}),-1.0]])]})])]}),"instanceName":"2"});
            var Q3;
            Q3=makeQuery(id+"F6.opPattern","COPY",BODY,{"derivedFrom":makeQuery(id+"F3.opLoft","SWEPT_BODY",BODY,{"disambiguationData":[OSD([makeQuery(id+"F0.imprint","IMPRINT",FACE,{"disambiguationData":[TD([[makeQuery(id+"F0.imprint","IMPRINT",EDGE,{"derivedFrom":sQuery(id+"F0.wireOp",EDGE,"E1")}),1.0]])]}),makeQuery(id+"F2.imprint","IMPRINT",FACE,{"disambiguationData":[TD([[makeQuery(id+"F2.imprint","IMPRINT",EDGE,{"derivedFrom":sQuery(id+"F2.wireOp",EDGE,"E22.1.0")}),-1.0]])]})])]}),"instanceName":"3"});
            var Q4;
            Q4=makeQuery(id+"F6.opPattern","COPY",BODY,{"derivedFrom":makeQuery(id+"F3.opLoft","SWEPT_BODY",BODY,{"disambiguationData":[OSD([makeQuery(id+"F0.imprint","IMPRINT",FACE,{"disambiguationData":[TD([[makeQuery(id+"F0.imprint","IMPRINT",EDGE,{"derivedFrom":sQuery(id+"F0.wireOp",EDGE,"E1")}),1.0]])]}),makeQuery(id+"F2.imprint","IMPRINT",FACE,{"disambiguationData":[TD([[makeQuery(id+"F2.imprint","IMPRINT",EDGE,{"derivedFrom":sQuery(id+"F2.wireOp",EDGE,"E22.1.0")}),-1.0]])]})])]}),"instanceName":"4"});
            var Q5;
            Q5=makeQuery(id+"F6.opPattern","COPY",BODY,{"derivedFrom":makeQuery(id+"F3.opLoft","SWEPT_BODY",BODY,{"disambiguationData":[OSD([makeQuery(id+"F0.imprint","IMPRINT",FACE,{"disambiguationData":[TD([[makeQuery(id+"F0.imprint","IMPRINT",EDGE,{"derivedFrom":sQuery(id+"F0.wireOp",EDGE,"E1")}),1.0]])]}),makeQuery(id+"F2.imprint","IMPRINT",FACE,{"disambiguationData":[TD([[makeQuery(id+"F2.imprint","IMPRINT",EDGE,{"derivedFrom":sQuery(id+"F2.wireOp",EDGE,"E22.1.0")}),-1.0]])]})])]}),"instanceName":"5"});
            var Q6;
            Q6=makeQuery(id+"F6.opPattern","COPY",BODY,{"derivedFrom":makeQuery(id+"F3.opLoft","SWEPT_BODY",BODY,{"disambiguationData":[OSD([makeQuery(id+"F0.imprint","IMPRINT",FACE,{"disambiguationData":[TD([[makeQuery(id+"F0.imprint","IMPRINT",EDGE,{"derivedFrom":sQuery(id+"F0.wireOp",EDGE,"E1")}),1.0]])]}),makeQuery(id+"F2.imprint","IMPRINT",FACE,{"disambiguationData":[TD([[makeQuery(id+"F2.imprint","IMPRINT",EDGE,{"derivedFrom":sQuery(id+"F2.wireOp",EDGE,"E22.1.0")}),-1.0]])]})])]}),"instanceName":"6"});
            var Q7;
            Q7=makeQuery(id+"F6.opPattern","COPY",BODY,{"derivedFrom":makeQuery(id+"F3.opLoft","SWEPT_BODY",BODY,{"disambiguationData":[OSD([makeQuery(id+"F0.imprint","IMPRINT",FACE,{"disambiguationData":[TD([[makeQuery(id+"F0.imprint","IMPRINT",EDGE,{"derivedFrom":sQuery(id+"F0.wireOp",EDGE,"E1")}),1.0]])]}),makeQuery(id+"F2.imprint","IMPRINT",FACE,{"disambiguationData":[TD([[makeQuery(id+"F2.imprint","IMPRINT",EDGE,{"derivedFrom":sQuery(id+"F2.wireOp",EDGE,"E22.1.0")}),-1.0]])]})])]}),"instanceName":"7"});
            var Q8;
            Q8=makeQuery(id+"F6.opPattern","COPY",BODY,{"derivedFrom":makeQuery(id+"F3.opLoft","SWEPT_BODY",BODY,{"disambiguationData":[OSD([makeQuery(id+"F0.imprint","IMPRINT",FACE,{"disambiguationData":[TD([[makeQuery(id+"F0.imprint","IMPRINT",EDGE,{"derivedFrom":sQuery(id+"F0.wireOp",EDGE,"E1")}),1.0]])]}),makeQuery(id+"F2.imprint","IMPRINT",FACE,{"disambiguationData":[TD([[makeQuery(id+"F2.imprint","IMPRINT",EDGE,{"derivedFrom":sQuery(id+"F2.wireOp",EDGE,"E22.1.0")}),-1.0]])]})])]}),"instanceName":"8"});
            var Q9;
            Q9=makeQuery(id+"F6.opPattern","COPY",BODY,{"derivedFrom":makeQuery(id+"F3.opLoft","SWEPT_BODY",BODY,{"disambiguationData":[OSD([makeQuery(id+"F0.imprint","IMPRINT",FACE,{"disambiguationData":[TD([[makeQuery(id+"F0.imprint","IMPRINT",EDGE,{"derivedFrom":sQuery(id+"F0.wireOp",EDGE,"E1")}),1.0]])]}),makeQuery(id+"F2.imprint","IMPRINT",FACE,{"disambiguationData":[TD([[makeQuery(id+"F2.imprint","IMPRINT",EDGE,{"derivedFrom":sQuery(id+"F2.wireOp",EDGE,"E22.1.0")}),-1.0]])]})])]}),"instanceName":"9"});
            var Q10;
            Q10=makeQuery(id+"F6.opPattern","COPY",BODY,{"derivedFrom":makeQuery(id+"F3.opLoft","SWEPT_BODY",BODY,{"disambiguationData":[OSD([makeQuery(id+"F0.imprint","IMPRINT",FACE,{"disambiguationData":[TD([[makeQuery(id+"F0.imprint","IMPRINT",EDGE,{"derivedFrom":sQuery(id+"F0.wireOp",EDGE,"E1")}),1.0]])]}),makeQuery(id+"F2.imprint","IMPRINT",FACE,{"disambiguationData":[TD([[makeQuery(id+"F2.imprint","IMPRINT",EDGE,{"derivedFrom":sQuery(id+"F2.wireOp",EDGE,"E22.1.0")}),-1.0]])]})])]}),"instanceName":"10"});
            var Q11;
            Q11=makeQuery(id+"F6.opPattern","COPY",BODY,{"derivedFrom":makeQuery(id+"F3.opLoft","SWEPT_BODY",BODY,{"disambiguationData":[OSD([makeQuery(id+"F0.imprint","IMPRINT",FACE,{"disambiguationData":[TD([[makeQuery(id+"F0.imprint","IMPRINT",EDGE,{"derivedFrom":sQuery(id+"F0.wireOp",EDGE,"E1")}),1.0]])]}),makeQuery(id+"F2.imprint","IMPRINT",FACE,{"disambiguationData":[TD([[makeQuery(id+"F2.imprint","IMPRINT",EDGE,{"derivedFrom":sQuery(id+"F2.wireOp",EDGE,"E22.1.0")}),-1.0]])]})])]}),"instanceName":"11"});
            var Q12;
            Q12=makeQuery(id+"F6.opPattern","COPY",BODY,{"derivedFrom":makeQuery(id+"F3.opLoft","SWEPT_BODY",BODY,{"disambiguationData":[OSD([makeQuery(id+"F0.imprint","IMPRINT",FACE,{"disambiguationData":[TD([[makeQuery(id+"F0.imprint","IMPRINT",EDGE,{"derivedFrom":sQuery(id+"F0.wireOp",EDGE,"E1")}),1.0]])]}),makeQuery(id+"F2.imprint","IMPRINT",FACE,{"disambiguationData":[TD([[makeQuery(id+"F2.imprint","IMPRINT",EDGE,{"derivedFrom":sQuery(id+"F2.wireOp",EDGE,"E22.1.0")}),-1.0]])]})])]}),"instanceName":"12"});
            var Q13;
            Q13=makeQuery(id+"F6.opPattern","COPY",BODY,{"derivedFrom":makeQuery(id+"F3.opLoft","SWEPT_BODY",BODY,{"disambiguationData":[OSD([makeQuery(id+"F0.imprint","IMPRINT",FACE,{"disambiguationData":[TD([[makeQuery(id+"F0.imprint","IMPRINT",EDGE,{"derivedFrom":sQuery(id+"F0.wireOp",EDGE,"E1")}),1.0]])]}),makeQuery(id+"F2.imprint","IMPRINT",FACE,{"disambiguationData":[TD([[makeQuery(id+"F2.imprint","IMPRINT",EDGE,{"derivedFrom":sQuery(id+"F2.wireOp",EDGE,"E22.1.0")}),-1.0]])]})])]}),"instanceName":"13"});
            var Q14;
            Q14=makeQuery(id+"F6.opPattern","COPY",BODY,{"derivedFrom":makeQuery(id+"F3.opLoft","SWEPT_BODY",BODY,{"disambiguationData":[OSD([makeQuery(id+"F0.imprint","IMPRINT",FACE,{"disambiguationData":[TD([[makeQuery(id+"F0.imprint","IMPRINT",EDGE,{"derivedFrom":sQuery(id+"F0.wireOp",EDGE,"E1")}),1.0]])]}),makeQuery(id+"F2.imprint","IMPRINT",FACE,{"disambiguationData":[TD([[makeQuery(id+"F2.imprint","IMPRINT",EDGE,{"derivedFrom":sQuery(id+"F2.wireOp",EDGE,"E22.1.0")}),-1.0]])]})])]}),"instanceName":"14"});
            var Q15;
            Q15=makeQuery(id+"F6.opPattern","COPY",BODY,{"derivedFrom":makeQuery(id+"F3.opLoft","SWEPT_BODY",BODY,{"disambiguationData":[OSD([makeQuery(id+"F0.imprint","IMPRINT",FACE,{"disambiguationData":[TD([[makeQuery(id+"F0.imprint","IMPRINT",EDGE,{"derivedFrom":sQuery(id+"F0.wireOp",EDGE,"E1")}),1.0]])]}),makeQuery(id+"F2.imprint","IMPRINT",FACE,{"disambiguationData":[TD([[makeQuery(id+"F2.imprint","IMPRINT",EDGE,{"derivedFrom":sQuery(id+"F2.wireOp",EDGE,"E22.1.0")}),-1.0]])]})])]}),"instanceName":"15"});
            var Q16;
            Q16=makeQuery(id+"F6.opPattern","COPY",BODY,{"derivedFrom":makeQuery(id+"F3.opLoft","SWEPT_BODY",BODY,{"disambiguationData":[OSD([makeQuery(id+"F0.imprint","IMPRINT",FACE,{"disambiguationData":[TD([[makeQuery(id+"F0.imprint","IMPRINT",EDGE,{"derivedFrom":sQuery(id+"F0.wireOp",EDGE,"E1")}),1.0]])]}),makeQuery(id+"F2.imprint","IMPRINT",FACE,{"disambiguationData":[TD([[makeQuery(id+"F2.imprint","IMPRINT",EDGE,{"derivedFrom":sQuery(id+"F2.wireOp",EDGE,"E22.1.0")}),-1.0]])]})])]}),"instanceName":"16"});
            var Q17;
            Q17=makeQuery(id+"F6.opPattern","COPY",BODY,{"derivedFrom":makeQuery(id+"F3.opLoft","SWEPT_BODY",BODY,{"disambiguationData":[OSD([makeQuery(id+"F0.imprint","IMPRINT",FACE,{"disambiguationData":[TD([[makeQuery(id+"F0.imprint","IMPRINT",EDGE,{"derivedFrom":sQuery(id+"F0.wireOp",EDGE,"E1")}),1.0]])]}),makeQuery(id+"F2.imprint","IMPRINT",FACE,{"disambiguationData":[TD([[makeQuery(id+"F2.imprint","IMPRINT",EDGE,{"derivedFrom":sQuery(id+"F2.wireOp",EDGE,"E22.1.0")}),-1.0]])]})])]}),"instanceName":"17"});
            var Q18;
            Q18=makeQuery(id+"F6.opPattern","COPY",BODY,{"derivedFrom":makeQuery(id+"F3.opLoft","SWEPT_BODY",BODY,{"disambiguationData":[OSD([makeQuery(id+"F0.imprint","IMPRINT",FACE,{"disambiguationData":[TD([[makeQuery(id+"F0.imprint","IMPRINT",EDGE,{"derivedFrom":sQuery(id+"F0.wireOp",EDGE,"E1")}),1.0]])]}),makeQuery(id+"F2.imprint","IMPRINT",FACE,{"disambiguationData":[TD([[makeQuery(id+"F2.imprint","IMPRINT",EDGE,{"derivedFrom":sQuery(id+"F2.wireOp",EDGE,"E22.1.0")}),-1.0]])]})])]}),"instanceName":"19"});
            var Q19;
            Q19=makeQuery(id+"F6.opPattern","COPY",BODY,{"derivedFrom":makeQuery(id+"F3.opLoft","SWEPT_BODY",BODY,{"disambiguationData":[OSD([makeQuery(id+"F0.imprint","IMPRINT",FACE,{"disambiguationData":[TD([[makeQuery(id+"F0.imprint","IMPRINT",EDGE,{"derivedFrom":sQuery(id+"F0.wireOp",EDGE,"E1")}),1.0]])]}),makeQuery(id+"F2.imprint","IMPRINT",FACE,{"disambiguationData":[TD([[makeQuery(id+"F2.imprint","IMPRINT",EDGE,{"derivedFrom":sQuery(id+"F2.wireOp",EDGE,"E22.1.0")}),-1.0]])]})])]}),"instanceName":"20"});
            var Q20;
            Q20=makeQuery(id+"F6.opPattern","COPY",BODY,{"derivedFrom":makeQuery(id+"F3.opLoft","SWEPT_BODY",BODY,{"disambiguationData":[OSD([makeQuery(id+"F0.imprint","IMPRINT",FACE,{"disambiguationData":[TD([[makeQuery(id+"F0.imprint","IMPRINT",EDGE,{"derivedFrom":sQuery(id+"F0.wireOp",EDGE,"E1")}),1.0]])]}),makeQuery(id+"F2.imprint","IMPRINT",FACE,{"disambiguationData":[TD([[makeQuery(id+"F2.imprint","IMPRINT",EDGE,{"derivedFrom":sQuery(id+"F2.wireOp",EDGE,"E22.1.0")}),-1.0]])]})])]}),"instanceName":"21"});
            var Q21;
            Q21=makeQuery(id+"F6.opPattern","COPY",BODY,{"derivedFrom":makeQuery(id+"F3.opLoft","SWEPT_BODY",BODY,{"disambiguationData":[OSD([makeQuery(id+"F0.imprint","IMPRINT",FACE,{"disambiguationData":[TD([[makeQuery(id+"F0.imprint","IMPRINT",EDGE,{"derivedFrom":sQuery(id+"F0.wireOp",EDGE,"E1")}),1.0]])]}),makeQuery(id+"F2.imprint","IMPRINT",FACE,{"disambiguationData":[TD([[makeQuery(id+"F2.imprint","IMPRINT",EDGE,{"derivedFrom":sQuery(id+"F2.wireOp",EDGE,"E22.1.0")}),-1.0]])]})])]}),"instanceName":"22"});
            var Q22;
            Q22=makeQuery(id+"F6.opPattern","COPY",BODY,{"derivedFrom":makeQuery(id+"F3.opLoft","SWEPT_BODY",BODY,{"disambiguationData":[OSD([makeQuery(id+"F0.imprint","IMPRINT",FACE,{"disambiguationData":[TD([[makeQuery(id+"F0.imprint","IMPRINT",EDGE,{"derivedFrom":sQuery(id+"F0.wireOp",EDGE,"E1")}),1.0]])]}),makeQuery(id+"F2.imprint","IMPRINT",FACE,{"disambiguationData":[TD([[makeQuery(id+"F2.imprint","IMPRINT",EDGE,{"derivedFrom":sQuery(id+"F2.wireOp",EDGE,"E22.1.0")}),-1.0]])]})])]}),"instanceName":"23"});
            var Q23;
            Q23=makeQuery(id+"F6.opPattern","COPY",BODY,{"derivedFrom":makeQuery(id+"F3.opLoft","SWEPT_BODY",BODY,{"disambiguationData":[OSD([makeQuery(id+"F0.imprint","IMPRINT",FACE,{"disambiguationData":[TD([[makeQuery(id+"F0.imprint","IMPRINT",EDGE,{"derivedFrom":sQuery(id+"F0.wireOp",EDGE,"E1")}),1.0]])]}),makeQuery(id+"F2.imprint","IMPRINT",FACE,{"disambiguationData":[TD([[makeQuery(id+"F2.imprint","IMPRINT",EDGE,{"derivedFrom":sQuery(id+"F2.wireOp",EDGE,"E22.1.0")}),-1.0]])]})])]}),"instanceName":"18"});
            booleanBodies(context, id + "F7", {"operationType" : BooleanOperationType.UNION, "tools" : qUnion([Q0, Q1, Q2, Q3, Q4, Q5, Q6, Q7, Q8, Q9, Q10, Q11, Q12, Q13, Q14, Q15, Q16, Q17, Q18, Q19, Q20, Q21, Q22, Q23])});
        }
        {
            var Q0;
            {var subQ3=makeQuery(id+"F5.boolean.opBoolean","MERGE",FACE,{"derivedFrom":[makeQuery(id+"F3.opLoft","CAP_FACE",FACE,{"disambiguationData":[OSD([makeQuery(id+"F2.imprint","IMPRINT",FACE,{"disambiguationData":[TD([[makeQuery(id+"F2.imprint","IMPRINT",EDGE,{"derivedFrom":sQuery(id+"F2.wireOp",EDGE,"E22.1.0")}),-1.0]])]})])],"isStart":true}),makeQuery(id+"F5.opExtrude","CAP_FACE",FACE,{"disambiguationData":[OSD([sQuery(id+"F4.wireOp",EDGE,"E23")])],"isStart":true})]});Q0=makeQuery(id+"F7.opBoolean","MERGE",FACE,{"derivedFrom":[subQ3,makeQuery(id+"F6.opPattern","COPY",FACE,{"derivedFrom":subQ3,"instanceName":"1"}),makeQuery(id+"F6.opPattern","COPY",FACE,{"derivedFrom":subQ3,"instanceName":"2"}),makeQuery(id+"F6.opPattern","COPY",FACE,{"derivedFrom":subQ3,"instanceName":"3"}),makeQuery(id+"F6.opPattern","COPY",FACE,{"derivedFrom":subQ3,"instanceName":"4"}),makeQuery(id+"F6.opPattern","COPY",FACE,{"derivedFrom":subQ3,"instanceName":"5"}),makeQuery(id+"F6.opPattern","COPY",FACE,{"derivedFrom":subQ3,"instanceName":"6"}),makeQuery(id+"F6.opPattern","COPY",FACE,{"derivedFrom":subQ3,"instanceName":"7"}),makeQuery(id+"F6.opPattern","COPY",FACE,{"derivedFrom":subQ3,"instanceName":"8"}),makeQuery(id+"F6.opPattern","COPY",FACE,{"derivedFrom":subQ3,"instanceName":"9"}),makeQuery(id+"F6.opPattern","COPY",FACE,{"derivedFrom":subQ3,"instanceName":"10"}),makeQuery(id+"F6.opPattern","COPY",FACE,{"derivedFrom":subQ3,"instanceName":"11"}),makeQuery(id+"F6.opPattern","COPY",FACE,{"derivedFrom":subQ3,"instanceName":"12"}),makeQuery(id+"F6.opPattern","COPY",FACE,{"derivedFrom":subQ3,"instanceName":"13"}),makeQuery(id+"F6.opPattern","COPY",FACE,{"derivedFrom":subQ3,"instanceName":"14"}),makeQuery(id+"F6.opPattern","COPY",FACE,{"derivedFrom":subQ3,"instanceName":"15"}),makeQuery(id+"F6.opPattern","COPY",FACE,{"derivedFrom":subQ3,"instanceName":"16"}),makeQuery(id+"F6.opPattern","COPY",FACE,{"derivedFrom":subQ3,"instanceName":"17"}),makeQuery(id+"F6.opPattern","COPY",FACE,{"derivedFrom":subQ3,"instanceName":"18"}),makeQuery(id+"F6.opPattern","COPY",FACE,{"derivedFrom":subQ3,"instanceName":"19"}),makeQuery(id+"F6.opPattern","COPY",FACE,{"derivedFrom":subQ3,"instanceName":"20"}),makeQuery(id+"F6.opPattern","COPY",FACE,{"derivedFrom":subQ3,"instanceName":"21"}),makeQuery(id+"F6.opPattern","COPY",FACE,{"derivedFrom":subQ3,"instanceName":"22"}),makeQuery(id+"F6.opPattern","COPY",FACE,{"derivedFrom":subQ3,"instanceName":"23"})]});}
            var sketch = newSketch(context, id + "F8", { "sketchPlane" : qUnion([Q0])});
            skCircle(sketch, "E24", {"center": v(0, 0) * mm, "radius": 6.35 * mm});
            skSolve(sketch);
        }
        {
            var Q0;
            Q0 = qSketchRegion(id + "F8", true);
            extrude(context, id + "F9", {"entities" : qUnion([Q0]), "operationType" : NewBodyOperationType.REMOVE, "endBound" : BoundingType.THROUGH_ALL, "oppositeDirection" : true, "depth" : 25.4 * mm});
        }
    });
